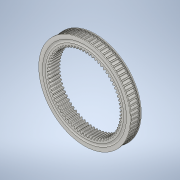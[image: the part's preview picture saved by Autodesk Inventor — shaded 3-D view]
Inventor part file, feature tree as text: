
AUTODESK INVENTOR PART (.ipt)
format: ipt  version: 2020 (Build 240168000, 168)  size: 1,221,632 bytes
history: native  units: mm (DEFAULTED — no unit token found)
features: sketch x5, plane x4, extrude x3, other x3, revolve x1, chamfer x1, mirror x1
ambient origin geometry x8: Origin, YZ Plane, XZ Plane, XY Plane, X Axis, Y Axis, Z Axis, Center Point
bodies: Solid1 (feature_tree)
feature tree (18):
  extrude  "Extrusion1"  Depth=14.0mm TaperAngle=0.0deg
  plane  "Work Plane1"
  plane  "Work Plane2"
  plane  "Work Plane3"
  other  "Spur Gear"
  extrude  "Extrusion2"  Depth=76.2mm TaperAngle=0.0deg
  extrude  "Extrusion3"  TaperAngle=0.0deg  [1 undecoded]
  revolve  "Revolution1"  [1 undecoded]
  plane  "Work Plane4"
  chamfer  "Chamfer1"  Distance=30.48mm
  mirror  "Mirror2"
  sketch  "Sketch1"  dims[d0=104.0765mm d1=14.0mm d2=0.0mm]
  sketch  "Sketch2"  dims[d3=91.44mm d4=76.2mm d5=0.0mm]
  other  "Srf1"
  sketch  "Sketch3"  dims[d6=0.0mm d7=0.436332mm d9=0.0mm]
  sketch  "Sketch4"  dims[d14=0.0mm d15=30.48mm d16=0.0mm d17=0.0mm d18=0.0mm d19=30.48mm]
  sketch  "Sketch6"  dims[d20=114.6mm d21=110.44mm d22=3.05mm d23=0.86mm d24=0.872665mm d25=720.0mm d27=360.0deg d29=0.001745mm d30=0.01mm d31=25.4mm d32=0.0mm d34=1.5mm d35=0.0mm d36=3.96875mm d37=0.79375mm d38=51.435mm d39=90.0deg d40=0.4mm d41=3.175mm d42=45.0deg d44=0.8mm]
  other  "Pitch Diameter"
note: 2 required parameter values undecoded (feature->parameter linkage not recoverable at this tier; creation-order binding heuristic only, values carry confidence <= 0.55)